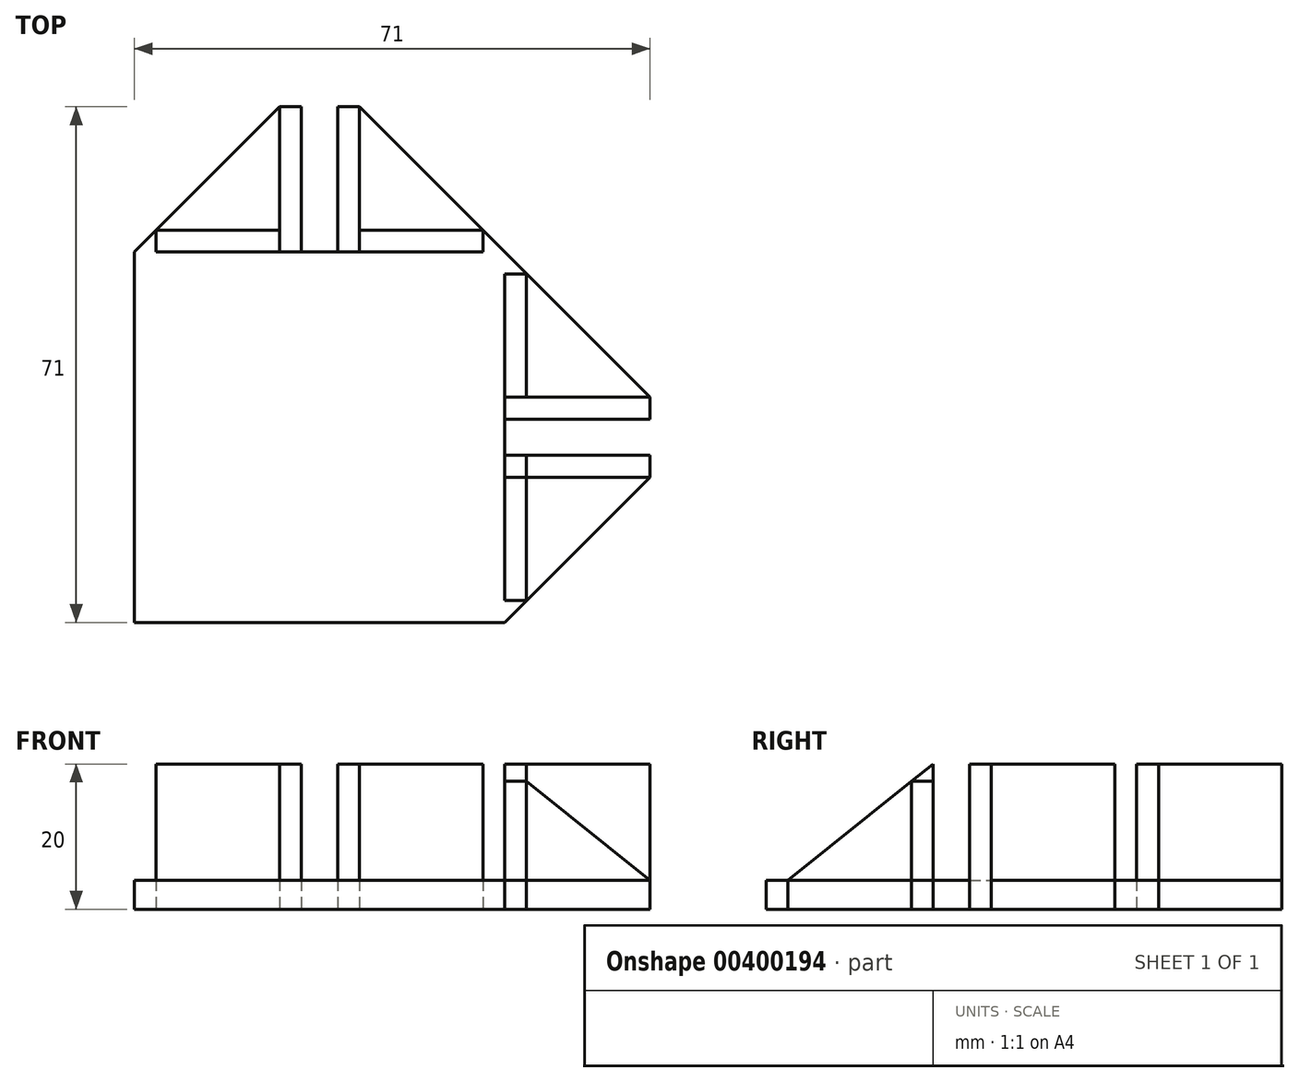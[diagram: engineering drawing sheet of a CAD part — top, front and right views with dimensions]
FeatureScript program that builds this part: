
annotation { "Feature Type Name" : "Feature", "Feature Type Description" : "" }
export const myFeature = defineFeature(function(context is Context, id is Id, definition is map)
    precondition{}
    {
        {
            var Q0;
            Q0=qCreatedBy(makeId("Top.planeOp"),FACE);
            var sketch = newSketch(context, id + "F0", { "sketchPlane" : qUnion([Q0])});
            skLineSegment(sketch, "E0.bottom", {"start": v(25.5, -25.5) * mm, "end": v(-25.5, -25.5) * mm});
            skLineSegment(sketch, "E0.top", {"start": v(25.5, 25.5) * mm, "end": v(-25.5, 25.5) * mm});
            skLineSegment(sketch, "E0.left", {"start": v(25.5, -25.5) * mm, "end": v(25.5, 25.5) * mm});
            skLineSegment(sketch, "E0.right", {"start": v(-25.5, -25.5) * mm, "end": v(-25.5, 25.5) * mm});
            skPoint(sketch, "E0.middle", {"position": v(0, 0) * mm});
            skLineSegment(sketch, "E1", {"start": v(-25.5, 25.5) * mm, "end": v(-5.5, 25.5) * mm});
            skLineSegment(sketch, "E2", {"start": v(-5.5, 25.5) * mm, "end": v(-5.5, 45.5) * mm});
            skLineSegment(sketch, "E3", {"start": v(-5.5, 45.5) * mm, "end": v(-25.5, 25.5) * mm});
            skLineSegment(sketch, "E4.MirrorCS", {"start": v(25.5, 25.5) * mm, "end": v(5.5, 25.5) * mm});
            skLineSegment(sketch, "E5.MirrorCS", {"start": v(5.5, 45.5) * mm, "end": v(25.5, 25.5) * mm});
            skLineSegment(sketch, "E6.MirrorCS", {"start": v(5.5, 25.5) * mm, "end": v(5.5, 45.5) * mm});
            skLineSegment(sketch, "E7", {"start": v(25.5, -25.5) * mm, "end": v(25.5, -5.5) * mm});
            skLineSegment(sketch, "E8", {"start": v(25.5, -5.5) * mm, "end": v(45.5, -5.5) * mm});
            skLineSegment(sketch, "E9", {"start": v(45.5, -5.5) * mm, "end": v(25.5, -25.5) * mm});
            skLineSegment(sketch, "E10.MirrorCS", {"start": v(45.5, 5.5) * mm, "end": v(25.5, 25.5) * mm});
            skLineSegment(sketch, "E11.MirrorCS", {"start": v(25.5, 5.5) * mm, "end": v(45.5, 5.5) * mm});
            skLineSegment(sketch, "E12.MirrorCS", {"start": v(25.5, 25.5) * mm, "end": v(25.5, 5.5) * mm});
            skSolve(sketch);
        }
        {
            var Q0;
            Q0=qSketchRegion(id+"F0",true);
            extrude(context, id + "F1", {"entities" : qUnion([Q0]), "depth" : 4 * mm});
        }
        {
            var Q0;
            Q0=qCreatedBy(makeId("Top.planeOp"),FACE);
            var sketch = newSketch(context, id + "F2", { "sketchPlane" : qUnion([Q0])});
            skLineSegment(sketch, "E13.0", {"start": v(-5.5, 25.5) * mm, "end": v(-5.5, 45.5) * mm});
            skLineSegment(sketch, "E13.1", {"start": v(5.5, 25.5) * mm, "end": v(-5.5, 25.5) * mm});
            skLineSegment(sketch, "E13.2", {"start": v(5.5, 25.5) * mm, "end": v(5.5, 45.5) * mm});
            skLineSegment(sketch, "E13.3", {"start": v(25.5, 5.5) * mm, "end": v(45.5, 5.5) * mm});
            skLineSegment(sketch, "E13.4", {"start": v(25.5, -5.5) * mm, "end": v(45.5, -5.5) * mm});
            skLineSegment(sketch, "E13.5", {"start": v(25.5, -5.5) * mm, "end": v(25.5, 5.5) * mm});
            skLineSegment(sketch, "E14", {"start": v(-5.5, 45.5) * mm, "end": v(-2.5, 45.5) * mm});
            skLineSegment(sketch, "E15", {"start": v(-2.5, 45.5) * mm, "end": v(-2.5, 25.5) * mm});
            skLineSegment(sketch, "E16.MirrorCS", {"start": v(5.5, 45.5) * mm, "end": v(2.5, 45.5) * mm});
            skLineSegment(sketch, "E17.MirrorCS", {"start": v(2.5, 45.5) * mm, "end": v(2.5, 25.5) * mm});
            skLineSegment(sketch, "E18", {"start": v(45.5, 5.5) * mm, "end": v(45.5, 2.5) * mm});
            skLineSegment(sketch, "E19", {"start": v(45.5, 2.5) * mm, "end": v(25.5, 2.5) * mm});
            skLineSegment(sketch, "E20.MirrorCS", {"start": v(45.5, -2.5) * mm, "end": v(25.5, -2.5) * mm});
            skLineSegment(sketch, "E21.MirrorCS", {"start": v(45.5, -5.5) * mm, "end": v(45.5, -2.5) * mm});
            skLineSegment(sketch, "E22", {"start": v(25.5, -2.5) * mm, "end": v(25.5, -22.5) * mm});
            skLineSegment(sketch, "E23", {"start": v(25.5, -22.5) * mm, "end": v(28.5, -22.5) * mm});
            skLineSegment(sketch, "E24", {"start": v(28.5, -22.5) * mm, "end": v(28.5, -5.5) * mm});
            skLineSegment(sketch, "E25.MirrorCS", {"start": v(25.5, 2.5) * mm, "end": v(25.5, 22.5) * mm});
            skLineSegment(sketch, "E26.MirrorCS", {"start": v(28.5, 22.5) * mm, "end": v(28.5, 5.5) * mm});
            skLineSegment(sketch, "E27.MirrorCS", {"start": v(25.5, 22.5) * mm, "end": v(28.5, 22.5) * mm});
            skLineSegment(sketch, "E28", {"start": v(5.5, 25.5) * mm, "end": v(22.5, 25.5) * mm});
            skLineSegment(sketch, "E29", {"start": v(22.5, 25.5) * mm, "end": v(22.5, 28.5) * mm});
            skLineSegment(sketch, "E30", {"start": v(22.5, 28.5) * mm, "end": v(5.5, 28.5) * mm});
            skLineSegment(sketch, "E31.MirrorCS", {"start": v(-22.5, 28.5) * mm, "end": v(-5.5, 28.5) * mm});
            skLineSegment(sketch, "E32.MirrorCS", {"start": v(-22.5, 25.5) * mm, "end": v(-22.5, 28.5) * mm});
            skLineSegment(sketch, "E33.MirrorCS", {"start": v(-5.5, 25.5) * mm, "end": v(-22.5, 25.5) * mm});
            skSolve(sketch);
        }
        {
            var Q0;
            {var subQ4=sQuery(id+"F2.wireOp",EDGE,"E23");Q0=makeQuery(id+"F2.imprint","IMPRINT",FACE,{"disambiguationData":[TD([[makeQuery(id+"F2.imprint","IMPRINT",EDGE,{"derivedFrom":subQ4}),1.0]])]});}
            var Q1;
            {var subQ3=sQuery(id+"F2.wireOp",EDGE,"E26.MirrorCS");Q1=makeQuery(id+"F2.imprint","IMPRINT",FACE,{"disambiguationData":[TD([[makeQuery(id+"F2.imprint","IMPRINT",EDGE,{"derivedFrom":subQ3}),-1.0]])]});}
            var Q2;
            {var subQ0=sQuery(id+"F2.wireOp",EDGE,"E28");Q2=makeQuery(id+"F2.imprint","IMPRINT",FACE,{"disambiguationData":[TD([[makeQuery(id+"F2.imprint","IMPRINT",EDGE,{"derivedFrom":subQ0}),1.0]])]});}
            var Q3;
            {var subQ2=sQuery(id+"F2.wireOp",EDGE,"E31.MirrorCS");Q3=makeQuery(id+"F2.imprint","IMPRINT",FACE,{"disambiguationData":[TD([[makeQuery(id+"F2.imprint","IMPRINT",EDGE,{"derivedFrom":subQ2}),-1.0]])]});}
            extrude(context, id + "F3", {"entities" : qUnion([Q0, Q1, Q2, Q3]), "depth" : 20 * mm});
        }
        {
            var Q0;
            {var subQ1=sQuery(id+"F2.wireOp",EDGE,"E18");Q0=makeQuery(id+"F2.imprint","IMPRINT",FACE,{"disambiguationData":[TD([[makeQuery(id+"F2.imprint","IMPRINT",EDGE,{"derivedFrom":subQ1}),-1.0]])]});}
            var Q1;
            {var subQ1=sQuery(id+"F2.wireOp",EDGE,"E20.MirrorCS");Q1=makeQuery(id+"F2.imprint","IMPRINT",FACE,{"disambiguationData":[TD([[makeQuery(id+"F2.imprint","IMPRINT",EDGE,{"derivedFrom":subQ1}),1.0]])]});}
            var Q2;
            {var subQ0=sQuery(id+"F2.wireOp",EDGE,"E16.MirrorCS");Q2=makeQuery(id+"F2.imprint","IMPRINT",FACE,{"disambiguationData":[TD([[makeQuery(id+"F2.imprint","IMPRINT",EDGE,{"derivedFrom":subQ0}),1.0]])]});}
            var Q3;
            {var subQ0=sQuery(id+"F2.wireOp",EDGE,"E14");Q3=makeQuery(id+"F2.imprint","IMPRINT",FACE,{"disambiguationData":[TD([[makeQuery(id+"F2.imprint","IMPRINT",EDGE,{"derivedFrom":subQ0}),-1.0]])]});}
            extrude(context, id + "F4", {"entities" : qUnion([Q0, Q1, Q2, Q3]), "depth" : 20 * mm});
        }
        {
            var Q0;
            Q0=makeQuery(id+"F3.opExtrude","SWEPT_FACE",FACE,{"disambiguationData":[OSD([sQuery(id+"F2.wireOp",EDGE,"E22")])]});
            var sketch = newSketch(context, id + "F5", { "sketchPlane" : qUnion([Q0])});
            skLineSegment(sketch, "E34.0", {"start": v(25.5, 4) * mm, "end": v(-25.5, 4) * mm, "construction": true});
            skLineSegment(sketch, "E34.1", {"start": v(22.5, 20) * mm, "end": v(22.5, 0) * mm, "construction": true});
            skLineSegment(sketch, "E34.2", {"start": v(5.5, 20) * mm, "end": v(22.5, 20) * mm, "construction": true});
            skLineSegment(sketch, "E34.3", {"start": v(2.5, 20) * mm, "end": v(5.5, 20) * mm, "construction": true});
            skLineSegment(sketch, "E34.4", {"start": v(2.5, 20) * mm, "end": v(2.5, 0) * mm, "construction": true});
            skLineSegment(sketch, "E35", {"start": v(2.5, 20) * mm, "end": v(22.5, 4) * mm});
            skLineSegment(sketch, "E36", {"start": v(22.5, 4) * mm, "end": v(22.5, 20) * mm});
            skLineSegment(sketch, "E37", {"start": v(22.5, 20) * mm, "end": v(2.5, 20) * mm});
            skSolve(sketch);
        }
        {
            var Q0;
            {var subQ0=sQuery(id+"F5.wireOp",EDGE,"E37");var subQ1=sQuery(id+"F5.wireOp",EDGE,"E35");var subQ2=makeQuery(id+"F5.imprint","INTERSECT",VERTEX,{"derivedFrom":[subQ1,subQ0]});Q0=makeQuery(id+"F5.imprint","IMPRINT",FACE,{"disambiguationData":[TD([[makeQuery(id+"F5.imprint","IMPRINT",EDGE,{"disambiguationData":[TD([[subQ2,-1.0]])],"derivedFrom":subQ1}),1.0]])]});}
            var Q1;
            {var subQ0=sQuery(id+"F5.wireOp",EDGE,"E36");Q1=makeQuery(id+"F5.imprint","IMPRINT",FACE,{"disambiguationData":[TD([[makeQuery(id+"F5.imprint","IMPRINT",EDGE,{"derivedFrom":subQ0}),-1.0]])]});}
            var Q2;
            Q2=makeQuery(id+"F3.opExtrude","SWEPT_FACE",FACE,{"disambiguationData":[OSD([sQuery(id+"F2.wireOp",EDGE,"E24")])]});
            extrude(context, id + "F6", {"entities" : qUnion([Q0, Q1]), "operationType" : NewBodyOperationType.REMOVE, "endBound" : BoundingType.UP_TO_SURFACE, "oppositeDirection" : true, "endBoundEntityFace" : qUnion([Q2]), "depth" : 25 * mm});
        }
        {
            var Q0;
            Q0=makeQuery(id+"F4.opExtrude","SWEPT_FACE",FACE,{"disambiguationData":[OSD([sQuery(id+"F2.wireOp",EDGE,"E13.4")])]});
            var sketch = newSketch(context, id + "F7", { "sketchPlane" : qUnion([Q0])});
            skLineSegment(sketch, "E38.0", {"start": v(25.5, 20) * mm, "end": v(45.5, 20) * mm, "construction": true});
            skLineSegment(sketch, "E38.1", {"start": v(45.5, 20) * mm, "end": v(45.5, 0) * mm, "construction": true});
            skLineSegment(sketch, "E38.2", {"start": v(45.5, 4) * mm, "end": v(25.5, 4) * mm, "construction": true});
            skLineSegment(sketch, "E38.3", {"start": v(25.5, 20) * mm, "end": v(25.5, 0) * mm, "construction": true});
            skLineSegment(sketch, "E39", {"start": v(25.5, 20) * mm, "end": v(45.5, 4) * mm});
            skLineSegment(sketch, "E40", {"start": v(25.5, 4) * mm, "end": v(25.5, 20) * mm});
            skLineSegment(sketch, "E41", {"start": v(25.5, 4) * mm, "end": v(45.5, 4) * mm});
            skSolve(sketch);
        }
        {
            var Q0;
            {var subQ0=sQuery(id+"F7.wireOp",EDGE,"E39");Q0=makeQuery(id+"F7.imprint","IMPRINT",FACE,{"disambiguationData":[TD([[makeQuery(id+"F7.imprint","IMPRINT",EDGE,{"derivedFrom":subQ0}),1.0]])]});}
            var Q1;
            Q1=makeQuery(id+"F4.opExtrude","SWEPT_FACE",FACE,{"disambiguationData":[OSD([sQuery(id+"F2.wireOp",EDGE,"E20.MirrorCS")])]});
            extrude(context, id + "F8", {"entities" : qUnion([Q0]), "operationType" : NewBodyOperationType.REMOVE, "endBound" : BoundingType.UP_TO_SURFACE, "oppositeDirection" : true, "endBoundEntityFace" : qUnion([Q1]), "depth" : 25 * mm});
        }
    });
